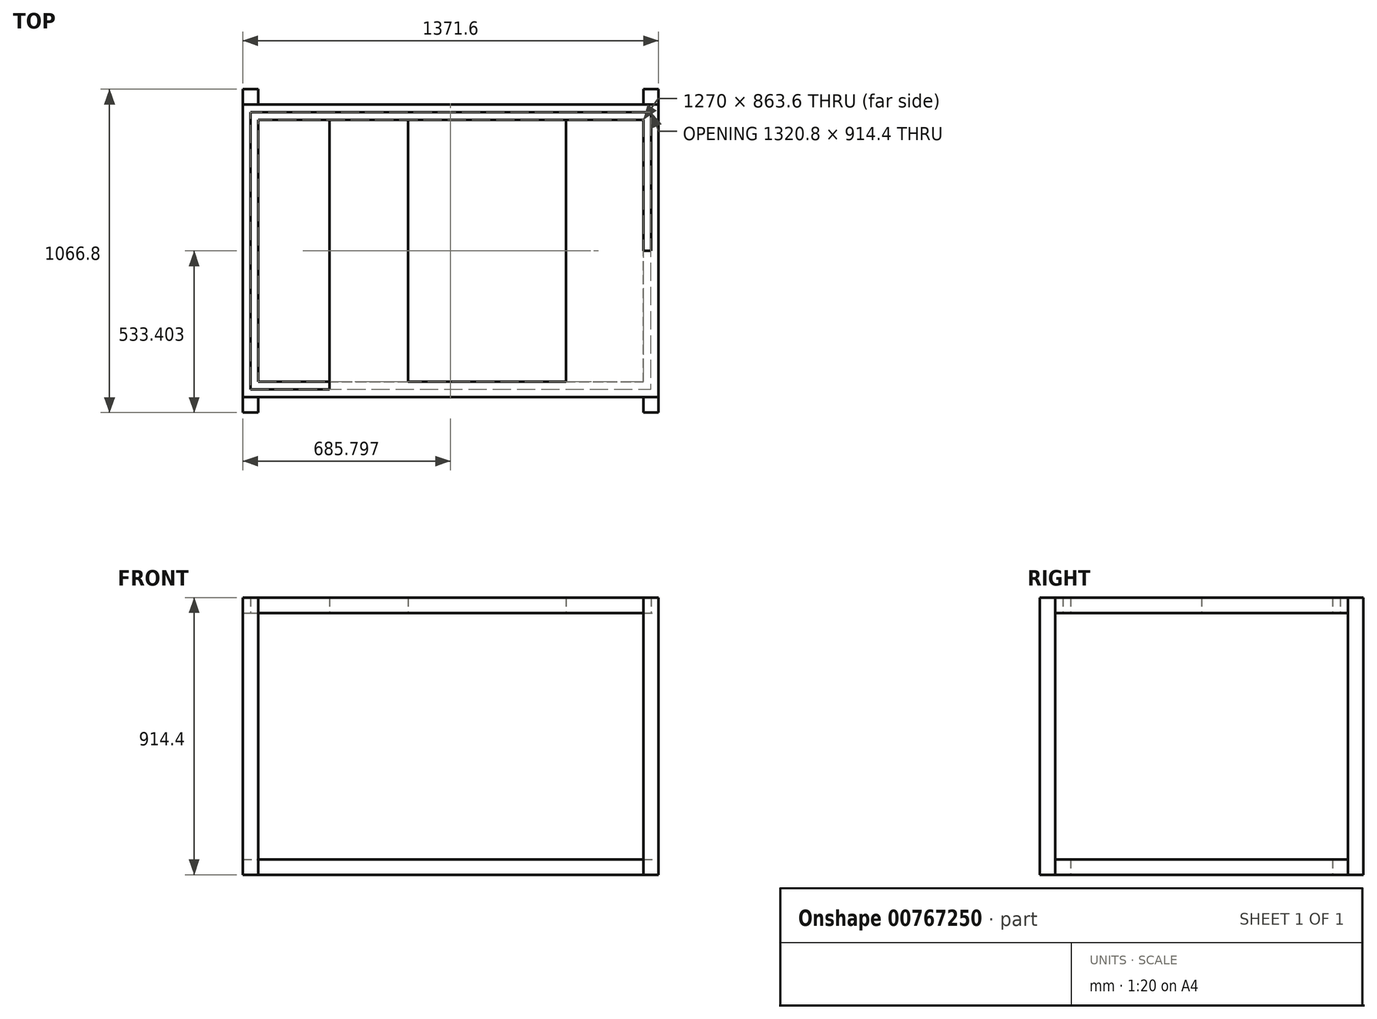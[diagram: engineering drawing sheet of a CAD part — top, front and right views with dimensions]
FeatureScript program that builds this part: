
annotation { "Feature Type Name" : "Feature", "Feature Type Description" : "" }
export const myFeature = defineFeature(function(context is Context, id is Id, definition is map)
    precondition{}
    {
        {
            var Q0;
            Q0=qCreatedBy(makeId("Top.planeOp"),FACE);
            var sketch = newSketch(context, id + "F0", { "sketchPlane" : qUnion([Q0])});
            skLineSegment(sketch, "E0.top", {"start": v(-1076.73, -350.62) * mm, "end": v(244.07, -350.62) * mm});
            skLineSegment(sketch, "E1.right", {"start": v(244.07, -350.62) * mm, "end": v(244.07, 563.78) * mm});
            skLineSegment(sketch, "E2.top", {"start": v(-1076.73, 563.78) * mm, "end": v(244.07, 563.78) * mm});
            skLineSegment(sketch, "E3.right", {"start": v(-1076.73, -350.62) * mm, "end": v(-1076.73, 563.78) * mm});
            skLineSegment(sketch, "E4.bottom", {"start": v(-1076.73, 563.78) * mm, "end": v(-816.38, 563.78) * mm});
            skLineSegment(sketch, "E4.top", {"start": v(-1076.73, -350.62) * mm, "end": v(-816.38, -350.62) * mm});
            skLineSegment(sketch, "E4.left", {"start": v(-1076.73, 563.78) * mm, "end": v(-1076.73, -350.62) * mm});
            skLineSegment(sketch, "E4.right", {"start": v(-816.38, 538.38) * mm, "end": v(-816.38, -350.62) * mm});
            skLineSegment(sketch, "E5.bottom", {"start": v(-816.38, 563.78) * mm, "end": v(-556.03, 563.78) * mm});
            skLineSegment(sketch, "E5.top", {"start": v(-816.38, -350.62) * mm, "end": v(-556.03, -350.62) * mm});
            skLineSegment(sketch, "E5.left", {"start": v(-816.38, 538.38) * mm, "end": v(-816.38, -325.22) * mm});
            skLineSegment(sketch, "E5.right", {"start": v(-556.03, 538.38) * mm, "end": v(-556.03, -325.22) * mm});
            skLineSegment(sketch, "E6.bottom", {"start": v(-556.03, 563.78) * mm, "end": v(-295.68, 563.78) * mm});
            skLineSegment(sketch, "E6.top", {"start": v(-556.03, -350.62) * mm, "end": v(-295.68, -350.62) * mm});
            skLineSegment(sketch, "E6.left", {"start": v(-556.03, 538.38) * mm, "end": v(-556.03, -350.62) * mm});
            skLineSegment(sketch, "E6.right", {"start": v(-295.68, 538.38) * mm, "end": v(-295.68, -350.62) * mm});
            skLineSegment(sketch, "E7.bottom", {"start": v(-295.68, 563.78) * mm, "end": v(-35.33, 563.78) * mm});
            skLineSegment(sketch, "E7.top", {"start": v(-295.68, -350.62) * mm, "end": v(-35.33, -350.62) * mm});
            skLineSegment(sketch, "E7.left", {"start": v(-295.68, 538.38) * mm, "end": v(-295.68, -325.22) * mm});
            skLineSegment(sketch, "E7.right", {"start": v(-35.33, 538.38) * mm, "end": v(-35.33, -325.22) * mm});
            skLineSegment(sketch, "E8.top", {"start": v(-1051.33, 335.18) * mm, "end": v(218.67, 335.18) * mm});
            skLineSegment(sketch, "E8.left", {"start": v(-1076.73, 563.78) * mm, "end": v(-1076.73, 335.18) * mm});
            skLineSegment(sketch, "E8.right", {"start": v(244.07, 563.78) * mm, "end": v(244.07, 335.18) * mm});
            skLineSegment(sketch, "E9.top", {"start": v(-1051.33, 106.58) * mm, "end": v(218.67, 106.58) * mm});
            skLineSegment(sketch, "E9.left", {"start": v(-1076.73, 335.18) * mm, "end": v(-1076.73, 106.58) * mm});
            skLineSegment(sketch, "E9.right", {"start": v(244.07, 335.18) * mm, "end": v(244.07, 106.58) * mm});
            skLineSegment(sketch, "E10.bottom", {"start": v(-1051.33, 106.58) * mm, "end": v(244.07, 106.58) * mm});
            skLineSegment(sketch, "E10.top", {"start": v(-1051.33, -122.02) * mm, "end": v(218.67, -122.02) * mm});
            skLineSegment(sketch, "E10.left", {"start": v(-1076.73, 106.58) * mm, "end": v(-1076.73, -122.02) * mm});
            skLineSegment(sketch, "E10.right", {"start": v(244.07, 106.58) * mm, "end": v(244.07, -122.02) * mm});
            skPoint(sketch, "E11.orphan", {"position": v(-1152.93, 563.78) * mm});
            skLineSegment(sketch, "E12.0", {"start": v(-1051.33, 538.38) * mm, "end": v(218.67, 538.38) * mm});
            skLineSegment(sketch, "E12.1", {"start": v(-1051.33, 538.38) * mm, "end": v(-1051.33, -325.22) * mm});
            skLineSegment(sketch, "E12.2", {"start": v(-1051.33, -325.22) * mm, "end": v(218.67, -325.22) * mm});
            skLineSegment(sketch, "E12.3", {"start": v(218.67, -325.22) * mm, "end": v(218.67, 538.38) * mm});
            skLineSegment(sketch, "E13.0", {"start": v(-1102.13, 589.18) * mm, "end": v(269.47, 589.18) * mm});
            skLineSegment(sketch, "E13.1", {"start": v(-1102.13, 589.18) * mm, "end": v(-1102.13, -376.02) * mm});
            skLineSegment(sketch, "E13.2", {"start": v(-1102.13, -376.02) * mm, "end": v(269.47, -376.02) * mm});
            skLineSegment(sketch, "E13.3", {"start": v(269.47, -376.02) * mm, "end": v(269.47, 589.18) * mm});
            skLineSegment(sketch, "E14.0", {"start": v(-1051.33, 81.18) * mm, "end": v(218.67, 81.18) * mm});
            skLineSegment(sketch, "E15.0", {"start": v(-1051.33, 131.98) * mm, "end": v(218.67, 131.98) * mm});
            skSolve(sketch);
        }
        {
            var Q0;
            Q0 = qSketchRegion(id + "F0", true);
            var Q1;
            Q1=makeQuery(id+"F0.imprint","IMPRINT",FACE,{"disambiguationData":[TD([[makeQuery(id+"F0.imprint","IMPRINT",EDGE,{"derivedFrom":sQuery(id+"F0.wireOp",EDGE,"E4.top")}),1.0]])]});
            var Q2;
            Q2=makeQuery(id+"F0.imprint","IMPRINT",FACE,{"disambiguationData":[TD([[makeQuery(id+"F0.imprint","IMPRINT",EDGE,{"derivedFrom":sQuery(id+"F0.wireOp",EDGE,"E0.top")}),1.0]])]});
            var Q3;
            {var subQ0=sQuery(id+"F0.wireOp",EDGE,"E6.top");Q3=makeQuery(id+"F0.imprint","IMPRINT",FACE,{"disambiguationData":[TD([[makeQuery(id+"F0.imprint","IMPRINT",EDGE,{"derivedFrom":subQ0}),1.0]])]});}
            var Q4;
            {var subQ0=sQuery(id+"F0.wireOp",EDGE,"E4.right");Q4=makeQuery(id+"F0.imprint","IMPRINT",FACE,{"disambiguationData":[TD([[makeQuery(id+"F0.imprint","IMPRINT",EDGE,{"derivedFrom":subQ0}),1.0]])]});}
            var Q5;
            {var subQ0=sQuery(id+"F0.wireOp",EDGE,"E15.0");var subQ1=sQuery(id+"F0.wireOp",EDGE,"E5.left");var subQ2=makeQuery(id+"F0.imprint","INTERSECT",VERTEX,{"derivedFrom":[subQ1,subQ0]});Q5=makeQuery(id+"F0.imprint","IMPRINT",FACE,{"disambiguationData":[TD([[makeQuery(id+"F0.imprint","IMPRINT",EDGE,{"disambiguationData":[TD([[subQ2,-1.0]])],"derivedFrom":subQ1}),-1.0]])]});}
            var Q6;
            {var subQ0=sQuery(id+"F0.wireOp",EDGE,"E15.0");var subQ1=sQuery(id+"F0.wireOp",EDGE,"E5.left");var subQ2=makeQuery(id+"F0.imprint","INTERSECT",VERTEX,{"derivedFrom":[subQ1,subQ0]});Q6=makeQuery(id+"F0.imprint","IMPRINT",FACE,{"disambiguationData":[TD([[makeQuery(id+"F0.imprint","IMPRINT",EDGE,{"disambiguationData":[TD([[subQ2,-1.0]])],"derivedFrom":subQ1}),1.0]])]});}
            var Q7;
            {var subQ0=sQuery(id+"F0.wireOp",EDGE,"E15.0");var subQ1=sQuery(id+"F0.wireOp",EDGE,"E6.left");var subQ2=makeQuery(id+"F0.imprint","INTERSECT",VERTEX,{"derivedFrom":[subQ1,subQ0]});Q7=makeQuery(id+"F0.imprint","IMPRINT",FACE,{"disambiguationData":[TD([[makeQuery(id+"F0.imprint","IMPRINT",EDGE,{"disambiguationData":[TD([[subQ2,-1.0]])],"derivedFrom":subQ1}),1.0]])]});}
            var Q8;
            {var subQ0=sQuery(id+"F0.wireOp",EDGE,"E15.0");var subQ1=sQuery(id+"F0.wireOp",EDGE,"E7.left");var subQ2=makeQuery(id+"F0.imprint","INTERSECT",VERTEX,{"derivedFrom":[subQ1,subQ0]});Q8=makeQuery(id+"F0.imprint","IMPRINT",FACE,{"disambiguationData":[TD([[makeQuery(id+"F0.imprint","IMPRINT",EDGE,{"disambiguationData":[TD([[subQ2,-1.0]])],"derivedFrom":subQ1}),1.0]])]});}
            var Q9;
            {var subQ0=sQuery(id+"F0.wireOp",EDGE,"E15.0");var subQ1=sQuery(id+"F0.wireOp",EDGE,"E7.right");var subQ2=makeQuery(id+"F0.imprint","INTERSECT",VERTEX,{"derivedFrom":[subQ1,subQ0]});Q9=makeQuery(id+"F0.imprint","IMPRINT",FACE,{"disambiguationData":[TD([[makeQuery(id+"F0.imprint","IMPRINT",EDGE,{"disambiguationData":[TD([[subQ2,-1.0]])],"derivedFrom":subQ1}),1.0]])]});}
            var Q10;
            {var subQ0=sQuery(id+"F0.wireOp",EDGE,"E10.bottom");var subQ1=sQuery(id+"F0.wireOp",EDGE,"E5.left");var subQ2=makeQuery(id+"F0.imprint","INTERSECT",VERTEX,{"derivedFrom":[subQ1,subQ0]});Q10=makeQuery(id+"F0.imprint","IMPRINT",FACE,{"disambiguationData":[TD([[makeQuery(id+"F0.imprint","IMPRINT",EDGE,{"disambiguationData":[TD([[subQ2,-1.0]])],"derivedFrom":subQ1}),-1.0]])]});}
            var Q11;
            {var subQ0=sQuery(id+"F0.wireOp",EDGE,"E10.bottom");var subQ1=sQuery(id+"F0.wireOp",EDGE,"E5.left");var subQ2=makeQuery(id+"F0.imprint","INTERSECT",VERTEX,{"derivedFrom":[subQ1,subQ0]});Q11=makeQuery(id+"F0.imprint","IMPRINT",FACE,{"disambiguationData":[TD([[makeQuery(id+"F0.imprint","IMPRINT",EDGE,{"disambiguationData":[TD([[subQ2,-1.0]])],"derivedFrom":subQ1}),1.0]])]});}
            var Q12;
            {var subQ0=sQuery(id+"F0.wireOp",EDGE,"E10.bottom");var subQ1=sQuery(id+"F0.wireOp",EDGE,"E6.left");var subQ2=makeQuery(id+"F0.imprint","INTERSECT",VERTEX,{"derivedFrom":[subQ1,subQ0]});Q12=makeQuery(id+"F0.imprint","IMPRINT",FACE,{"disambiguationData":[TD([[makeQuery(id+"F0.imprint","IMPRINT",EDGE,{"disambiguationData":[TD([[subQ2,-1.0]])],"derivedFrom":subQ1}),1.0]])]});}
            var Q13;
            {var subQ0=sQuery(id+"F0.wireOp",EDGE,"E10.bottom");var subQ1=sQuery(id+"F0.wireOp",EDGE,"E7.left");var subQ2=makeQuery(id+"F0.imprint","INTERSECT",VERTEX,{"derivedFrom":[subQ1,subQ0]});Q13=makeQuery(id+"F0.imprint","IMPRINT",FACE,{"disambiguationData":[TD([[makeQuery(id+"F0.imprint","IMPRINT",EDGE,{"disambiguationData":[TD([[subQ2,-1.0]])],"derivedFrom":subQ1}),1.0]])]});}
            var Q14;
            {var subQ0=sQuery(id+"F0.wireOp",EDGE,"E10.bottom");var subQ1=sQuery(id+"F0.wireOp",EDGE,"E7.right");var subQ2=makeQuery(id+"F0.imprint","INTERSECT",VERTEX,{"derivedFrom":[subQ1,subQ0]});Q14=makeQuery(id+"F0.imprint","IMPRINT",FACE,{"disambiguationData":[TD([[makeQuery(id+"F0.imprint","IMPRINT",EDGE,{"disambiguationData":[TD([[subQ2,-1.0]])],"derivedFrom":subQ1}),1.0]])]});}
            extrude(context, id + "F1", {"entities" : qUnion([Q0, Q1, Q2, Q3, Q4, Q5, Q6, Q7, Q8, Q9, Q10, Q11, Q12, Q13, Q14]), "depth" : 50.8 * mm, "offsetDistance" : 25.4 * mm});
        }
        {
            var Q0;
            Q0=makeQuery(id+"F1.opExtrude","CAP_FACE",FACE,{"disambiguationData":[OSD([sQuery(id+"F0.wireOp",EDGE,"E12.0"),sQuery(id+"F0.wireOp",EDGE,"E12.1"),sQuery(id+"F0.wireOp",EDGE,"E12.2"),sQuery(id+"F0.wireOp",EDGE,"E12.3"),sQuery(id+"F0.wireOp",EDGE,"E13.0"),sQuery(id+"F0.wireOp",EDGE,"E13.1"),sQuery(id+"F0.wireOp",EDGE,"E13.2"),sQuery(id+"F0.wireOp",EDGE,"E13.3")])],"isStart":false});
            var sketch = newSketch(context, id + "F2", { "sketchPlane" : qUnion([Q0])});
            skLineSegment(sketch, "E16.bottom", {"start": v(-1102.13, 589.18) * mm, "end": v(-1051.33, 589.18) * mm});
            skLineSegment(sketch, "E16.top", {"start": v(-1102.13, 639.98) * mm, "end": v(-1051.33, 639.98) * mm});
            skLineSegment(sketch, "E16.left", {"start": v(-1102.13, 589.18) * mm, "end": v(-1102.13, 639.98) * mm});
            skLineSegment(sketch, "E16.right", {"start": v(-1051.33, 589.18) * mm, "end": v(-1051.33, 639.98) * mm});
            skLineSegment(sketch, "E17.bottom", {"start": v(269.47, 589.18) * mm, "end": v(218.67, 589.18) * mm});
            skLineSegment(sketch, "E17.top", {"start": v(269.47, 639.98) * mm, "end": v(218.67, 639.98) * mm});
            skLineSegment(sketch, "E17.left", {"start": v(269.47, 589.18) * mm, "end": v(269.47, 639.98) * mm});
            skLineSegment(sketch, "E17.right", {"start": v(218.67, 589.18) * mm, "end": v(218.67, 639.98) * mm});
            skLineSegment(sketch, "E18.bottom", {"start": v(-1102.13, -376.02) * mm, "end": v(-1051.33, -376.02) * mm});
            skLineSegment(sketch, "E18.top", {"start": v(-1102.13, -426.82) * mm, "end": v(-1051.33, -426.82) * mm});
            skLineSegment(sketch, "E18.left", {"start": v(-1102.13, -376.02) * mm, "end": v(-1102.13, -426.82) * mm});
            skLineSegment(sketch, "E18.right", {"start": v(-1051.33, -376.02) * mm, "end": v(-1051.33, -426.82) * mm});
            skLineSegment(sketch, "E19.bottom", {"start": v(269.47, -376.02) * mm, "end": v(218.67, -376.02) * mm});
            skLineSegment(sketch, "E19.top", {"start": v(269.47, -426.82) * mm, "end": v(218.67, -426.82) * mm});
            skLineSegment(sketch, "E19.left", {"start": v(269.47, -376.02) * mm, "end": v(269.47, -426.82) * mm});
            skLineSegment(sketch, "E19.right", {"start": v(218.67, -376.02) * mm, "end": v(218.67, -426.82) * mm});
            skSolve(sketch);
        }
        {
            var Q0;
            Q0=makeQuery(id+"F2.imprint","IMPRINT",FACE,{"disambiguationData":[TD([[makeQuery(id+"F2.imprint","IMPRINT",EDGE,{"derivedFrom":sQuery(id+"F2.wireOp",EDGE,"E17.bottom")}),1.0]])]});
            var Q1;
            Q1=makeQuery(id+"F2.imprint","IMPRINT",FACE,{"disambiguationData":[TD([[makeQuery(id+"F2.imprint","IMPRINT",EDGE,{"derivedFrom":sQuery(id+"F2.wireOp",EDGE,"E18.bottom")}),-1.0]])]});
            var Q2;
            Q2=makeQuery(id+"F2.imprint","IMPRINT",FACE,{"disambiguationData":[TD([[makeQuery(id+"F2.imprint","IMPRINT",EDGE,{"derivedFrom":sQuery(id+"F2.wireOp",EDGE,"E19.bottom")}),-1.0]])]});
            var Q3;
            Q3=makeQuery(id+"F2.imprint","IMPRINT",FACE,{"disambiguationData":[TD([[makeQuery(id+"F2.imprint","IMPRINT",EDGE,{"derivedFrom":sQuery(id+"F2.wireOp",EDGE,"E16.bottom")}),1.0]])]});
            extrude(context, id + "F3", {"entities" : qUnion([Q0, Q1, Q2, Q3]), "depth" : -914.4 * mm, "offsetDistance" : 25.4 * mm});
        }
        {
            var Q0;
            Q0=makeQuery(id+"F3.opExtrude","CAP_FACE",FACE,{"disambiguationData":[OSD([sQuery(id+"F2.wireOp",EDGE,"E16.bottom"),sQuery(id+"F2.wireOp",EDGE,"E16.top"),sQuery(id+"F2.wireOp",EDGE,"E16.left"),sQuery(id+"F2.wireOp",EDGE,"E16.right")])],"isStart":false});
            var sketch = newSketch(context, id + "F4", { "sketchPlane" : qUnion([Q0])});
            skLineSegment(sketch, "E20.bottom", {"start": v(-1102.13, 376.02) * mm, "end": v(269.47, 376.02) * mm});
            skLineSegment(sketch, "E20.top", {"start": v(-1102.13, -589.18) * mm, "end": v(269.47, -589.18) * mm});
            skLineSegment(sketch, "E20.left", {"start": v(-1102.13, 376.02) * mm, "end": v(-1102.13, -589.18) * mm});
            skLineSegment(sketch, "E20.right", {"start": v(269.47, 376.02) * mm, "end": v(269.47, -589.18) * mm});
            skLineSegment(sketch, "E21.bottom", {"start": v(-1051.33, 325.22) * mm, "end": v(218.67, 325.22) * mm});
            skLineSegment(sketch, "E21.top", {"start": v(-1051.33, -538.38) * mm, "end": v(218.67, -538.38) * mm});
            skLineSegment(sketch, "E21.left", {"start": v(-1051.33, 325.22) * mm, "end": v(-1051.33, -538.38) * mm});
            skLineSegment(sketch, "E21.right", {"start": v(218.67, 325.22) * mm, "end": v(218.67, -538.38) * mm});
            skSolve(sketch);
        }
        {
            var Q0;
            Q0 = qSketchRegion(id + "F4", true);
            extrude(context, id + "F5", {"entities" : qUnion([Q0]), "depth" : -50.8 * mm, "offsetDistance" : 25.4 * mm});
        }
    });
